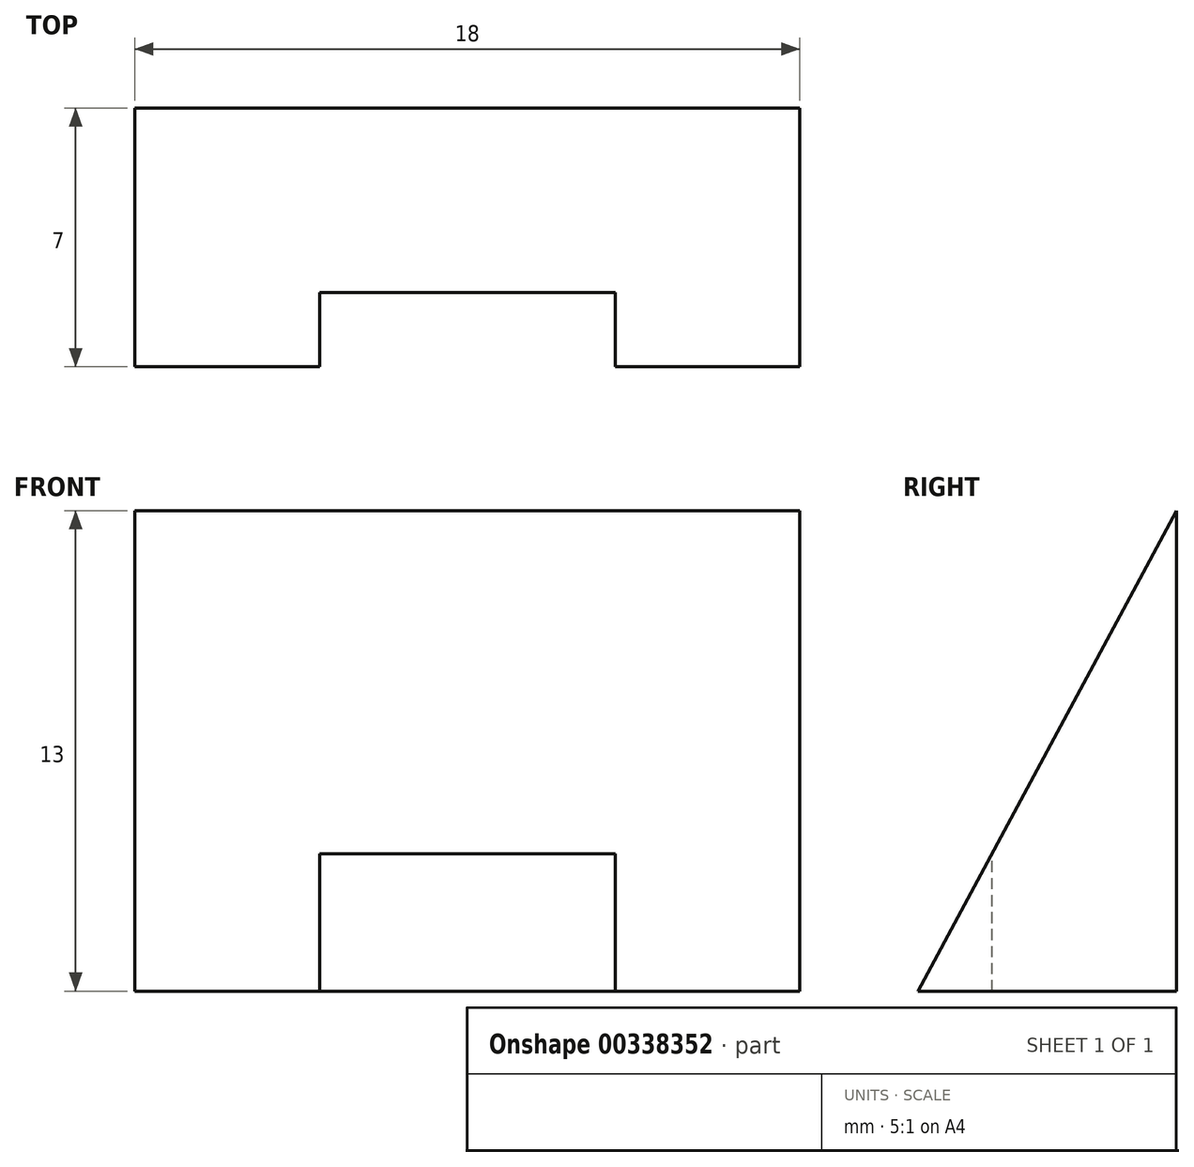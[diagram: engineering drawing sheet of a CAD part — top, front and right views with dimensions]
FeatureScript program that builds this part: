
annotation { "Feature Type Name" : "Feature", "Feature Type Description" : "" }
export const myFeature = defineFeature(function(context is Context, id is Id, definition is map)
    precondition{}
    {
        {
            var Q0;
            Q0=qCreatedBy(makeId("Top.planeOp"),FACE);
            var sketch = newSketch(context, id + "F0", { "sketchPlane" : qUnion([Q0])});
            skLineSegment(sketch, "E0.bottom", {"start": v(0, 0) * mm, "end": v(18, 0) * mm});
            skLineSegment(sketch, "E0.top", {"start": v(0, -7) * mm, "end": v(18, -7) * mm});
            skLineSegment(sketch, "E0.left", {"start": v(0, 0) * mm, "end": v(0, -7) * mm});
            skLineSegment(sketch, "E0.right", {"start": v(18, 0) * mm, "end": v(18, -7) * mm});
            skSolve(sketch);
        }
        {
            var Q0;
            Q0 = qSketchRegion(id + "F0", true);
            extrude(context, id + "F1", {"entities" : qUnion([Q0]), "depth" : 13 * mm});
        }
        {
            var Q0;
            Q0=makeQuery(id+"F1.opExtrude","CAP_FACE",FACE,{"disambiguationData":[OSD([sQuery(id+"F0.wireOp",EDGE,"E0.bottom"),sQuery(id+"F0.wireOp",EDGE,"E0.top"),sQuery(id+"F0.wireOp",EDGE,"E0.left"),sQuery(id+"F0.wireOp",EDGE,"E0.right")])],"isStart":false});
            var sketch = newSketch(context, id + "F2", { "sketchPlane" : qUnion([Q0])});
            skLineSegment(sketch, "E1.bottom", {"start": v(5, -7) * mm, "end": v(13, -7) * mm});
            skLineSegment(sketch, "E1.top", {"start": v(5, -5) * mm, "end": v(13, -5) * mm});
            skLineSegment(sketch, "E1.left", {"start": v(5, -7) * mm, "end": v(5, -5) * mm});
            skLineSegment(sketch, "E1.right", {"start": v(13, -7) * mm, "end": v(13, -5) * mm});
            skPoint(sketch, "E1.middle", {"position": v(9, -6) * mm});
            skPoint(sketch, "E1.middle.positionSnap0", {"position": v(9, -7) * mm});
            skPoint(sketch, "E1.centerSnap0", {"position": v(9, -7) * mm});
            skSolve(sketch);
        }
        {
            var Q0;
            Q0 = qSketchRegion(id + "F2", true);
            extrude(context, id + "F3", {"entities" : qUnion([Q0]), "operationType" : NewBodyOperationType.REMOVE, "endBound" : BoundingType.THROUGH_ALL, "oppositeDirection" : true, "depth" : 25 * mm});
        }
        {
            var Q0;
            Q0=makeQuery(id+"F1.opExtrude","SWEPT_FACE",FACE,{"disambiguationData":[OSD([sQuery(id+"F0.wireOp",EDGE,"E0.right")])]});
            var sketch = newSketch(context, id + "F4", { "sketchPlane" : qUnion([Q0])});
            skLineSegment(sketch, "E2", {"start": v(0, 13) * mm, "end": v(-7, 13) * mm});
            skLineSegment(sketch, "E3", {"start": v(-7, 13) * mm, "end": v(-7, 0) * mm});
            skLineSegment(sketch, "E4", {"start": v(-7, 0) * mm, "end": v(0, 13) * mm});
            skSolve(sketch);
        }
        {
            var Q0;
            Q0 = qSketchRegion(id + "F4", true);
            extrude(context, id + "F5", {"entities" : qUnion([Q0]), "operationType" : NewBodyOperationType.REMOVE, "endBound" : BoundingType.THROUGH_ALL, "oppositeDirection" : true, "depth" : 25 * mm});
        }
    });
